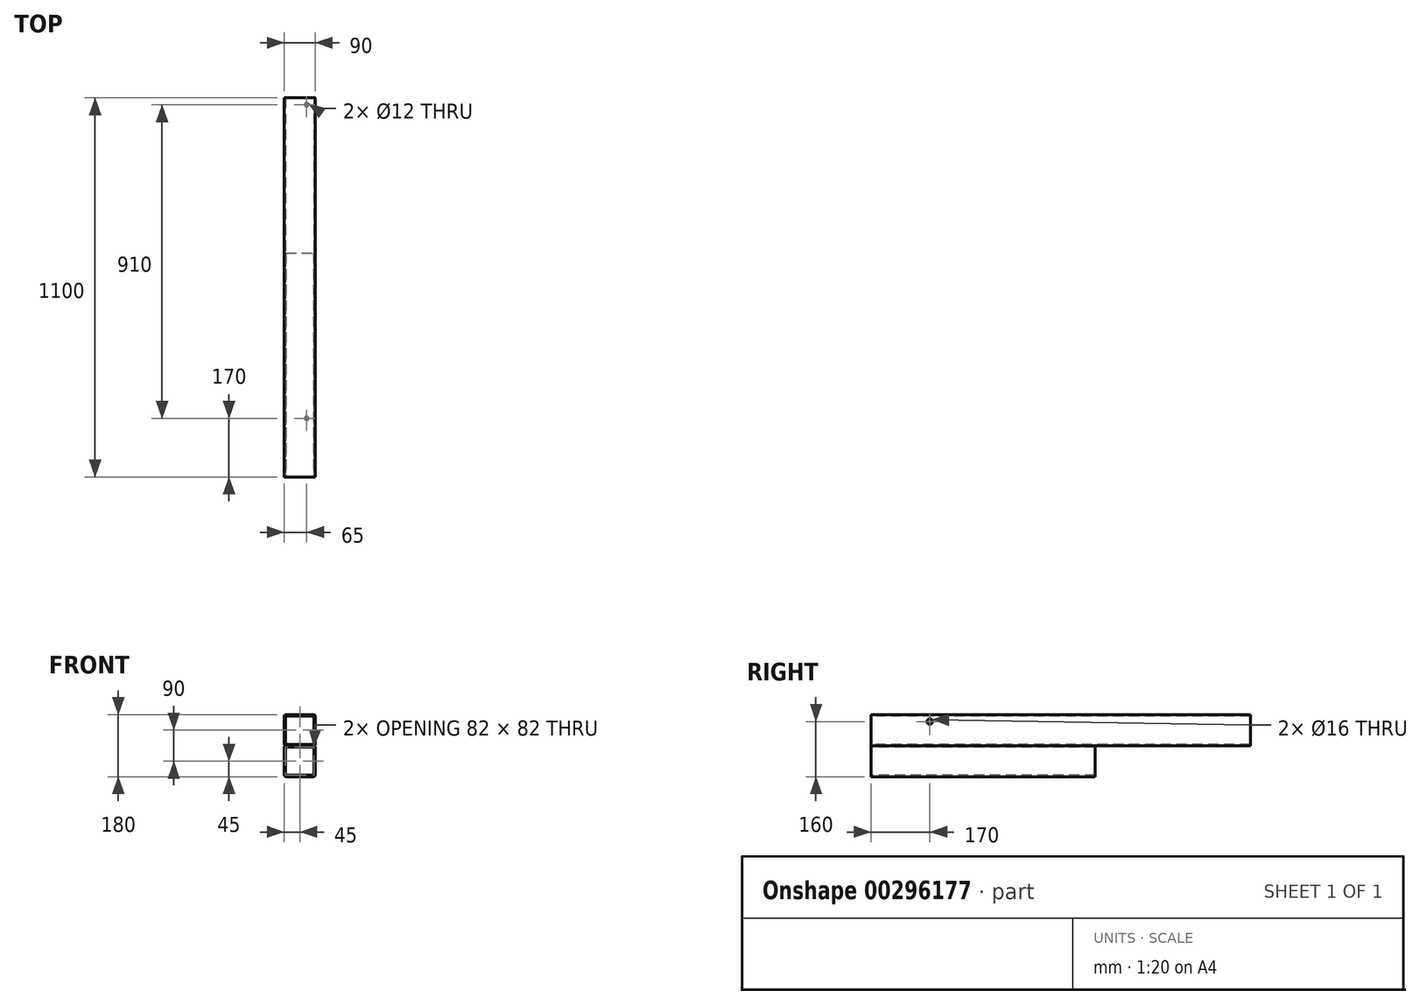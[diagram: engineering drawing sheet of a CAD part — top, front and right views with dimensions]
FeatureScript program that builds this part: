
annotation { "Feature Type Name" : "Feature", "Feature Type Description" : "" }
export const myFeature = defineFeature(function(context is Context, id is Id, definition is map)
    precondition{}
    {
        {
            var Q0;
            Q0=qCreatedBy(makeId("Front.planeOp"),FACE);
            var sketch = newSketch(context, id + "F0", { "sketchPlane" : qUnion([Q0])});
            skLineSegment(sketch, "E0.bottom", {"start": v(40, 45) * mm, "end": v(-40, 45) * mm});
            skLineSegment(sketch, "E0.top", {"start": v(40, -45) * mm, "end": v(-40, -45) * mm});
            skLineSegment(sketch, "E0.left", {"start": v(45, 40) * mm, "end": v(45, -40) * mm});
            skLineSegment(sketch, "E0.right", {"start": v(-45, 40) * mm, "end": v(-45, -40) * mm});
            skPoint(sketch, "E0.middle", {"position": v(0, 0) * mm});
            skPoint(sketch, "E1.visualSharp", {"position": v(-45, 45) * mm});
            skArc(sketch, "E1.filletArc", {"start": v(-40, 45) * mm, "mid": v(-43.54, 43.54) * mm, "end": v(-45, 40) * mm});
            skPoint(sketch, "E2.visualSharp", {"position": v(45, 45) * mm});
            skArc(sketch, "E2.filletArc", {"start": v(45, 40) * mm, "mid": v(43.54, 43.54) * mm, "end": v(40, 45) * mm});
            skPoint(sketch, "E3.visualSharp", {"position": v(45, -45) * mm});
            skArc(sketch, "E3.filletArc", {"start": v(40, -45) * mm, "mid": v(43.54, -43.54) * mm, "end": v(45, -40) * mm});
            skPoint(sketch, "E4.visualSharp", {"position": v(-45, -45) * mm});
            skArc(sketch, "E4.filletArc", {"start": v(-45, -40) * mm, "mid": v(-43.54, -43.54) * mm, "end": v(-40, -45) * mm});
            skArc(sketch, "E5.0", {"start": v(-40, 41) * mm, "mid": v(-40.7, 40.7) * mm, "end": v(-41, 40) * mm});
            skLineSegment(sketch, "E5.1", {"start": v(40, 41) * mm, "end": v(-40, 41) * mm});
            skLineSegment(sketch, "E5.2", {"start": v(-41, 40) * mm, "end": v(-41, -40) * mm});
            skArc(sketch, "E5.3", {"start": v(41, 40) * mm, "mid": v(40.7, 40.7) * mm, "end": v(40, 41) * mm});
            skArc(sketch, "E5.4", {"start": v(-41, -40) * mm, "mid": v(-40.7, -40.7) * mm, "end": v(-40, -41) * mm});
            skLineSegment(sketch, "E5.5", {"start": v(40, -41) * mm, "end": v(-40, -41) * mm});
            skArc(sketch, "E5.6", {"start": v(40, -41) * mm, "mid": v(40.7, -40.7) * mm, "end": v(41, -40) * mm});
            skLineSegment(sketch, "E5.7", {"start": v(41, 40) * mm, "end": v(41, -40) * mm});
            skLineSegment(sketch, "E6.top", {"start": v(40, -135) * mm, "end": v(-40, -135) * mm});
            skLineSegment(sketch, "E6.left", {"start": v(45, -50) * mm, "end": v(45, -130) * mm});
            skLineSegment(sketch, "E6.right", {"start": v(-45, -50) * mm, "end": v(-45, -130) * mm});
            skPoint(sketch, "E6.middle", {"position": v(0, -90) * mm});
            skArc(sketch, "E7.filletArc", {"start": v(-40, -45) * mm, "mid": v(-43.54, -46.46) * mm, "end": v(-45, -50) * mm});
            skArc(sketch, "E8.filletArc", {"start": v(45, -50) * mm, "mid": v(43.54, -46.46) * mm, "end": v(40, -45) * mm});
            skPoint(sketch, "E9.visualSharp", {"position": v(45, -135) * mm});
            skArc(sketch, "E9.filletArc", {"start": v(40, -135) * mm, "mid": v(43.54, -133.54) * mm, "end": v(45, -130) * mm});
            skPoint(sketch, "E10.visualSharp", {"position": v(-45, -135) * mm});
            skArc(sketch, "E10.filletArc", {"start": v(-45, -130) * mm, "mid": v(-43.54, -133.54) * mm, "end": v(-40, -135) * mm});
            skArc(sketch, "E11.0", {"start": v(-40, -49) * mm, "mid": v(-40.7, -49.3) * mm, "end": v(-41, -50) * mm});
            skLineSegment(sketch, "E11.1", {"start": v(40, -49) * mm, "end": v(-40, -49) * mm});
            skLineSegment(sketch, "E11.2", {"start": v(-41, -50) * mm, "end": v(-41, -130) * mm});
            skArc(sketch, "E11.3", {"start": v(41, -50) * mm, "mid": v(40.7, -49.3) * mm, "end": v(40, -49) * mm});
            skArc(sketch, "E11.4", {"start": v(-41, -130) * mm, "mid": v(-40.7, -130.7) * mm, "end": v(-40, -131) * mm});
            skLineSegment(sketch, "E11.5", {"start": v(40, -131) * mm, "end": v(-40, -131) * mm});
            skArc(sketch, "E11.6", {"start": v(40, -131) * mm, "mid": v(40.7, -130.7) * mm, "end": v(41, -130) * mm});
            skLineSegment(sketch, "E11.7", {"start": v(41, -50) * mm, "end": v(41, -130) * mm});
            skSolve(sketch);
        }
        {
            var Q0;
            Q0=makeQuery(id+"F0.imprint","IMPRINT",FACE,{"disambiguationData":[TD([[makeQuery(id+"F0.imprint","IMPRINT",EDGE,{"derivedFrom":sQuery(id+"F0.wireOp",EDGE,"E0.bottom")}),1.0]])]});
            var Q1;
            Q1=makeQuery(id+"F0.imprint","IMPRINT",FACE,{"disambiguationData":[TD([[makeQuery(id+"F0.imprint","IMPRINT",EDGE,{"derivedFrom":sQuery(id+"F0.wireOp",EDGE,"E0.top")}),1.0]])]});
            extrude(context, id + "F1", {"entities" : qUnion([Q0, Q1]), "oppositeDirection" : true, "depth" : 1100 * mm});
        }
        {
            var Q0;
            Q0=makeQuery(id+"F1.opExtrude","SWEPT_FACE",FACE,{"disambiguationData":[OSD([sQuery(id+"F0.wireOp",EDGE,"E0.left")])]});
            var sketch = newSketch(context, id + "F2", { "sketchPlane" : qUnion([Q0])});
            skCircle(sketch, "E12", {"center": v(170, 25) * mm, "radius": 8 * mm});
            skSolve(sketch);
        }
        {
            var Q0;
            Q0=makeQuery(id+"F2.imprint","IMPRINT",FACE,{"disambiguationData":[TD([[makeQuery(id+"F2.imprint","IMPRINT",EDGE,{"derivedFrom":sQuery(id+"F2.wireOp",EDGE,"E12")}),1.0]])]});
            extrude(context, id + "F3", {"entities" : qUnion([Q0]), "operationType" : NewBodyOperationType.REMOVE, "endBound" : BoundingType.THROUGH_ALL, "oppositeDirection" : true, "depth" : 25 * mm});
        }
        {
            var Q0;
            Q0=makeQuery(id+"F1.opExtrude","SWEPT_FACE",FACE,{"disambiguationData":[OSD([sQuery(id+"F0.wireOp",EDGE,"E6.left")])]});
            var sketch = newSketch(context, id + "F4", { "sketchPlane" : qUnion([Q0])});
            skLineSegment(sketch, "E13.bottom", {"start": v(650, -45) * mm, "end": v(1100, -45) * mm});
            skLineSegment(sketch, "E13.top", {"start": v(650, -135) * mm, "end": v(1100, -135) * mm});
            skLineSegment(sketch, "E13.left", {"start": v(650, -45) * mm, "end": v(650, -135) * mm});
            skLineSegment(sketch, "E13.right", {"start": v(1100, -45) * mm, "end": v(1100, -135) * mm});
            skSolve(sketch);
        }
        {
            var Q0;
            {var subQ0=sQuery(id+"F4.wireOp",EDGE,"E13.left");var subQ1=sQuery(id+"F0.wireOp",EDGE,"E6.left");var subQ2=makeQuery(id+"F1.opExtrude","SWEPT_EDGE",EDGE,{"disambiguationData":[OSD([subQ1,sQuery(id+"F0.wireOp",EDGE,"E8.filletArc")])]});var subQ3=makeQuery(id+"F4.imprint","INTERSECT",VERTEX,{"derivedFrom":[subQ2,subQ0]});Q0=makeQuery(id+"F4.imprint","IMPRINT",FACE,{"disambiguationData":[TD([[makeQuery(id+"F4.imprint","IMPRINT",EDGE,{"disambiguationData":[TD([[subQ3,-1.0]])],"derivedFrom":subQ0}),1.0]])]});}
            var Q1;
            {var subQ0=sQuery(id+"F4.wireOp",EDGE,"E13.bottom");Q1=makeQuery(id+"F4.imprint","IMPRINT",FACE,{"disambiguationData":[TD([[makeQuery(id+"F4.imprint","IMPRINT",EDGE,{"derivedFrom":subQ0}),-1.0]])]});}
            var Q2;
            {var subQ0=sQuery(id+"F4.wireOp",EDGE,"E13.top");Q2=makeQuery(id+"F4.imprint","IMPRINT",FACE,{"disambiguationData":[TD([[makeQuery(id+"F4.imprint","IMPRINT",EDGE,{"derivedFrom":subQ0}),1.0]])]});}
            extrude(context, id + "F5", {"entities" : qUnion([Q0, Q1, Q2]), "operationType" : NewBodyOperationType.REMOVE, "endBound" : BoundingType.THROUGH_ALL, "oppositeDirection" : true, "depth" : 25 * mm});
        }
        {
            var Q0;
            Q0=makeQuery(id+"F1.opExtrude","SWEPT_FACE",FACE,{"disambiguationData":[OSD([sQuery(id+"F0.wireOp",EDGE,"E6.top")])]});
            var sketch = newSketch(context, id + "F6", { "sketchPlane" : qUnion([Q0])});
            skCircle(sketch, "E14", {"center": v(20, -170) * mm, "radius": 6 * mm});
            skSolve(sketch);
        }
        {
            var Q0;
            Q0=makeQuery(id+"F6.imprint","IMPRINT",FACE,{"disambiguationData":[TD([[makeQuery(id+"F6.imprint","IMPRINT",EDGE,{"derivedFrom":sQuery(id+"F6.wireOp",EDGE,"E14")}),1.0]])]});
            extrude(context, id + "F7", {"entities" : qUnion([Q0]), "operationType" : NewBodyOperationType.REMOVE, "endBound" : BoundingType.UP_TO_NEXT, "oppositeDirection" : true, "depth" : 25 * mm});
        }
        {
            var Q0;
            Q0=makeQuery(id+"F5.boolean.opBoolean","COPY",FACE,{"derivedFrom":makeQuery(id+"F5.opExtrude","SWEPT_FACE",FACE,{"disambiguationData":[OSD([sQuery(id+"F4.wireOp",EDGE,"E13.bottom")])]})});
            var sketch = newSketch(context, id + "F8", { "sketchPlane" : qUnion([Q0])});
            skCircle(sketch, "E15", {"center": v(20, -1080) * mm, "radius": 6 * mm});
            skSolve(sketch);
        }
        {
            var Q0;
            Q0=makeQuery(id+"F8.imprint","IMPRINT",FACE,{"disambiguationData":[TD([[makeQuery(id+"F8.imprint","IMPRINT",EDGE,{"derivedFrom":sQuery(id+"F8.wireOp",EDGE,"E15")}),1.0]])]});
            extrude(context, id + "F9", {"entities" : qUnion([Q0]), "operationType" : NewBodyOperationType.REMOVE, "endBound" : BoundingType.UP_TO_NEXT, "oppositeDirection" : true, "depth" : 25 * mm});
        }
    });
